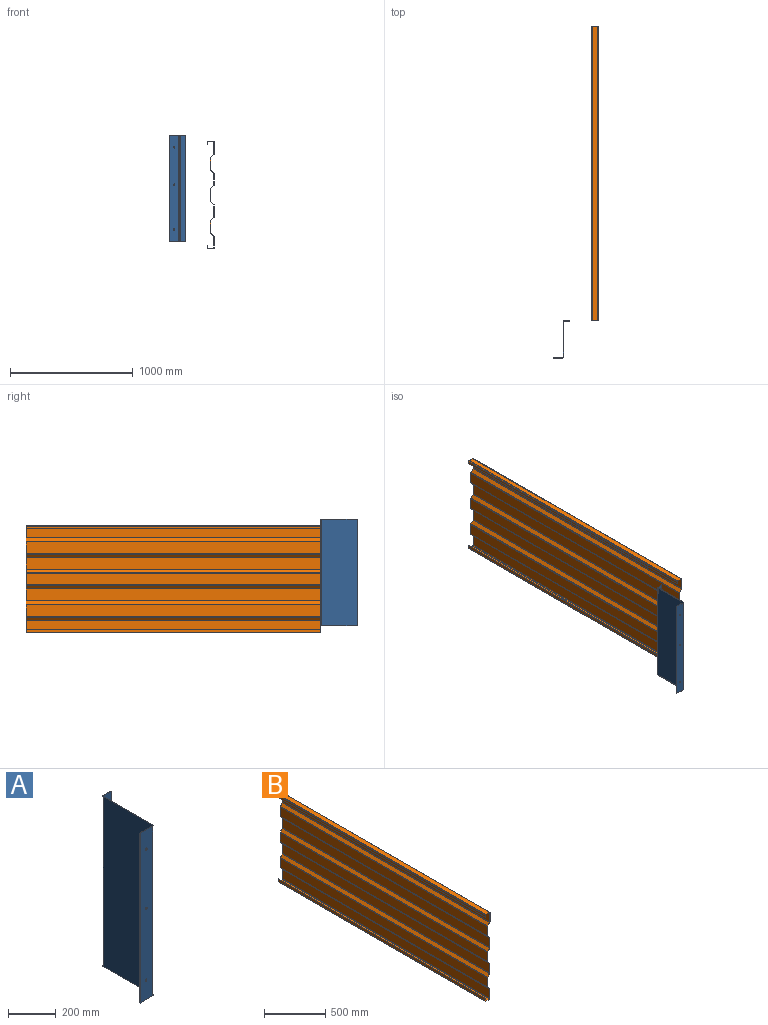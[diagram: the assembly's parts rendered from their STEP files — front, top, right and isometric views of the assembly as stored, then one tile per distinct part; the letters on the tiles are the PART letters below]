
ASSEMBLY  parts=2 mates=1
PART A: 25 faces, bbox 130x302x869 mm
  f0: plane 46x2mm, normal (0,0,-1), area 92mm2, adj f2,f3,f4,f22
  f1: plane 46x2mm, normal (0,0,1), area 92mm2, adj f2,f3,f4,f21
  f2: plane 869x2mm, normal (1,0,0), area 1738mm2, adj f0,f1,f3,f4
  f3: plane 869x46mm, normal (0,1,0), area 39974mm2, adj f0,f1,f2,f23
  f4: plane 869x46mm, normal (0,-1,0), area 39974mm2, adj f0,f1,f2,f24
  f5: plane 290x2mm, normal (0,0,-1), area 580mm2, adj f7,f8,f18,f22
  f6: plane 290x2mm, normal (0,0,1), area 580mm2, adj f7,f8,f17,f21
  f7: plane 869x290mm, normal (-1,0,0), area 252010mm2, adj f5,f6,f20,f23
  f8: plane 869x290mm, normal (1,0,0), area 252010mm2, adj f5,f6,f19,f24
  f9: plane 74x2mm, normal (0,0,-1), area 148mm2, adj f10,f15,f16,f18
  f10: plane 869x2mm, normal (-1,0,0), area 1738mm2, adj f9,f11,f15,f16
  f11: plane 74x2mm, normal (0,0,1), area 148mm2, adj f10,f15,f16,f17
  f12: cylinder r=5mm len=10mm, axis (0,1,0), area 62.8mm2, adj f15,f16
  f13: cylinder r=5mm len=10mm, axis (0,1,0), area 62.8mm2, adj f15,f16
  f14: cylinder r=5mm len=10mm, axis (0,1,0), area 62.8mm2, adj f15,f16
  f15: plane 869x74mm, normal (0,1,0), area 64070.4mm2, adj f9,f10,f11,f12,f13,f14,f20
  f16: plane 869x74mm, normal (0,-1,0), area 64070.4mm2, adj f9,f10,f11,f12,f13,f14,f19
  f17: plane 6x6mm, normal (0,0,1), area 15.7mm2, adj f6,f11,f19,f20
  f18: plane 6x6mm, normal (0,0,-1), area 15.7mm2, adj f5,f9,f19,f20
  f19: cylinder r=6mm len=869mm, axis (0,0,1), area 8190.1mm2, adj f8,f16,f17,f18
  f20: cylinder r=4mm len=869mm, axis (0,0,1), area 5460.1mm2, adj f7,f15,f17,f18
  f21: plane 6x6mm, normal (0,0,1), area 15.7mm2, adj f1,f6,f23,f24
  f22: plane 6x6mm, normal (0,0,-1), area 15.7mm2, adj f0,f5,f23,f24
  f23: cylinder r=6mm len=869mm, axis (0,0,1), area 8190.1mm2, adj f3,f7,f21,f22
  f24: cylinder r=4mm len=869mm, axis (0,0,1), area 5460.1mm2, adj f4,f8,f21,f22
PART B: 134 faces, bbox 55.5x2400x874.2 mm
  f0: plane 21x2.5mm, normal (0,1,0), area 52.5mm2, adj f2,f3,f4,f131
  f1: plane 21x2.5mm, normal (0,-1,0), area 52.5mm2, adj f2,f3,f4,f130
  f2: plane 2400x2.5mm, normal (0,0,-1), area 6000mm2, adj f0,f1,f3,f4
  f3: plane 2400x21mm, normal (1,0,0), area 50400mm2, adj f0,f1,f2,f133
  f4: plane 2400x21mm, normal (-1,0,0), area 50400mm2, adj f0,f1,f2,f132
  f5: plane 42x2.5mm, normal (0,1,0), area 105mm2, adj f7,f8,f127,f131
  f6: plane 42x2.5mm, normal (0,-1,0), area 105mm2, adj f7,f8,f126,f130
  f7: plane 2400x42mm, normal (0,0,-1), area 100800mm2, adj f5,f6,f129,f133
  f8: plane 2400x42mm, normal (0,0,1), area 100800mm2, adj f5,f6,f128,f132
  f9: plane 94.3x2.5mm, normal (0,1,0), area 235.8mm2, adj f11,f12,f123,f127
  f10: plane 94.3x2.5mm, normal (0,-1,0), area 235.8mm2, adj f11,f12,f122,f126
  f11: plane 2400x94.3mm, normal (-1,0,0), area 226325mm2, adj f9,f10,f125,f129
  f12: plane 2400x94.3mm, normal (1,0,0), area 226325mm2, adj f9,f10,f124,f128
  f13: plane 27.3x26.49mm, normal (0,1,0), area 88.9mm2, adj f15,f16,f119,f123
  f14: plane 27.3x26.49mm, normal (0,-1,0), area 88.9mm2, adj f15,f16,f118,f122
  f15: plane 2400x25.57mm, normal (-0.69,0,0.72), area 85303.2mm2, adj f13,f14,f120,f125
  f16: plane 2400x25.57mm, normal (0.69,0,-0.72), area 85303.2mm2, adj f13,f14,f121,f124
  f17: plane 94.55x2.5mm, normal (0,1,0), area 236.4mm2, adj f19,f20,f115,f119
  f18: plane 94.55x2.5mm, normal (0,-1,0), area 236.4mm2, adj f19,f20,f114,f118
  f19: plane 2400x94.55mm, normal (-1,0,0), area 226916.5mm2, adj f17,f18,f116,f120
  f20: plane 2400x94.55mm, normal (1,0,0), area 226916.5mm2, adj f17,f18,f117,f121
  f21: plane 26.98x26.98mm, normal (0,1,0), area 89.1mm2, adj f23,f24,f111,f115
  f22: plane 26.98x26.98mm, normal (0,-1,0), area 89.1mm2, adj f23,f24,f110,f114
  f23: plane 2400x25.21mm, normal (-0.71,0,-0.71), area 85561.8mm2, adj f21,f22,f113,f116
  f24: plane 2400x25.21mm, normal (0.71,0,0.71), area 85561.8mm2, adj f21,f22,f112,f117
  f25: plane 96.69x2.5mm, normal (0,1,0), area 241.7mm2, adj f27,f28,f107,f111
  f26: plane 96.69x2.5mm, normal (0,-1,0), area 241.7mm2, adj f27,f28,f106,f110
  f27: plane 2400x96.69mm, normal (-1,0,0), area 232047.1mm2, adj f25,f26,f109,f113
  f28: plane 2400x96.69mm, normal (1,0,0), area 232047.1mm2, adj f25,f26,f108,f112
  f29: plane 26.98x26.98mm, normal (0,1,0), area 89.1mm2, adj f31,f32,f103,f107
  f30: plane 26.98x26.98mm, normal (0,-1,0), area 89.1mm2, adj f31,f32,f102,f106
  f31: plane 2400x25.21mm, normal (-0.71,0,0.71), area 85561.8mm2, adj f29,f30,f104,f109
  f32: plane 2400x25.21mm, normal (0.71,0,-0.71), area 85561.8mm2, adj f29,f30,f105,f108
  f33: plane 94.62x2.5mm, normal (0,1,0), area 236.5mm2, adj f35,f36,f99,f103
  f34: plane 94.62x2.5mm, normal (0,-1,0), area 236.5mm2, adj f35,f36,f98,f102
  f35: plane 2400x94.62mm, normal (-1,0,0), area 227076.5mm2, adj f33,f34,f100,f104
  f36: plane 2400x94.62mm, normal (1,0,0), area 227076.5mm2, adj f33,f34,f101,f105
  f37: plane 26.98x26.98mm, normal (0,1,0), area 89.1mm2, adj f39,f40,f95,f99
  f38: plane 26.98x26.98mm, normal (0,-1,0), area 89.1mm2, adj f39,f40,f94,f98
  f39: plane 2400x25.21mm, normal (-0.71,0,-0.71), area 85561.8mm2, adj f37,f38,f97,f100
  f40: plane 2400x25.21mm, normal (0.71,0,0.71), area 85561.8mm2, adj f37,f38,f96,f101
  f41: plane 96.69x2.5mm, normal (0,1,0), area 241.7mm2, adj f43,f44,f91,f95
  f42: plane 96.69x2.5mm, normal (0,-1,0), area 241.7mm2, adj f43,f44,f90,f94
  f43: plane 2400x96.69mm, normal (-1,0,0), area 232047.1mm2, adj f41,f42,f93,f97
  f44: plane 2400x96.69mm, normal (1,0,0), area 232047.1mm2, adj f41,f42,f92,f96
  f45: plane 26.98x26.98mm, normal (0,1,0), area 89.1mm2, adj f47,f48,f87,f91
  f46: plane 26.98x26.98mm, normal (0,-1,0), area 89.1mm2, adj f47,f48,f86,f90
  f47: plane 2400x25.21mm, normal (-0.71,0,0.71), area 85561.8mm2, adj f45,f46,f88,f93
  f48: plane 2400x25.21mm, normal (0.71,0,-0.71), area 85561.8mm2, adj f45,f46,f89,f92
  f49: plane 94.62x2.5mm, normal (0,1,0), area 236.5mm2, adj f51,f52,f83,f87
  f50: plane 94.62x2.5mm, normal (0,-1,0), area 236.5mm2, adj f51,f52,f82,f86
  f51: plane 2400x94.62mm, normal (-1,0,0), area 227076.5mm2, adj f49,f50,f84,f88
  f52: plane 2400x94.62mm, normal (1,0,0), area 227076.5mm2, adj f49,f50,f85,f89
  f53: plane 26.98x26.98mm, normal (0,1,0), area 89.1mm2, adj f55,f56,f79,f83
  f54: plane 26.98x26.98mm, normal (0,-1,0), area 89.1mm2, adj f55,f56,f78,f82
  f55: plane 2400x25.21mm, normal (-0.71,0,-0.71), area 85561.8mm2, adj f53,f54,f81,f84
  f56: plane 2400x25.21mm, normal (0.71,0,0.71), area 85561.8mm2, adj f53,f54,f80,f85
  f57: plane 94.34x2.5mm, normal (0,1,0), area 235.9mm2, adj f59,f60,f75,f79
  f58: plane 94.34x2.5mm, normal (0,-1,0), area 235.9mm2, adj f59,f60,f74,f78
  f59: plane 2400x94.34mm, normal (-1,0,0), area 226423.6mm2, adj f57,f58,f77,f81
  f60: plane 2400x94.34mm, normal (1,0,0), area 226423.6mm2, adj f57,f58,f76,f80
  f61: plane 42x2.5mm, normal (0,1,0), area 105mm2, adj f63,f64,f71,f75
  f62: plane 42x2.5mm, normal (0,-1,0), area 105mm2, adj f63,f64,f70,f74
  f63: plane 2400x42mm, normal (0,0,1), area 100800mm2, adj f61,f62,f73,f77
  f64: plane 2400x42mm, normal (0,0,-1), area 100800mm2, adj f61,f62,f72,f76
  f65: plane 24.58x2.5mm, normal (0,1,0), area 61.4mm2, adj f66,f68,f69,f71
  f66: plane 2400x2.5mm, normal (0,0,1), area 6000mm2, adj f65,f67,f68,f69
  f67: plane 24.58x2.5mm, normal (0,-1,0), area 61.4mm2, adj f66,f68,f69,f70
  f68: plane 2400x24.58mm, normal (1,0,0), area 58991.7mm2, adj f65,f66,f67,f73
  f69: plane 2400x24.58mm, normal (-1,0,0), area 58991.7mm2, adj f65,f66,f67,f72
  f70: plane 6.5x6.5mm, normal (0,-1,0), area 20.6mm2, adj f62,f67,f72,f73
  f71: plane 6.5x6.5mm, normal (0,1,0), area 20.6mm2, adj f61,f65,f72,f73
  f72: cylinder r=6.5mm len=2400mm, axis (0,-1,0), area 24504.4mm2, adj f64,f69,f70,f71
  f73: cylinder r=4mm len=2400mm, axis (0,-1,0), area 15079.6mm2, adj f63,f68,f70,f71
  f74: plane 6.5x6.5mm, normal (0,-1,0), area 20.6mm2, adj f58,f62,f76,f77
  f75: plane 6.5x6.5mm, normal (0,1,0), area 20.6mm2, adj f57,f61,f76,f77
  f76: cylinder r=6.5mm len=2400mm, axis (0,-1,0), area 24504.4mm2, adj f60,f64,f74,f75
  f77: cylinder r=4mm len=2400mm, axis (0,-1,0), area 15079.6mm2, adj f59,f63,f74,f75
  f78: plane 4.6x3.67mm, normal (0,-1,0), area 10.3mm2, adj f54,f58,f80,f81
  f79: plane 4.6x3.67mm, normal (0,1,0), area 10.3mm2, adj f53,f57,f80,f81
  f80: cylinder r=6.5mm len=2400mm, axis (0,-1,0), area 12252.2mm2, adj f56,f60,f78,f79
  f81: cylinder r=4mm len=2400mm, axis (0,-1,0), area 7539.8mm2, adj f55,f59,f78,f79
  f82: plane 4.6x3.67mm, normal (0,-1,0), area 10.3mm2, adj f50,f54,f84,f85
  f83: plane 4.6x3.67mm, normal (0,1,0), area 10.3mm2, adj f49,f53,f84,f85
  f84: cylinder r=6.5mm len=2400mm, axis (0,-1,0), area 12252.2mm2, adj f51,f55,f82,f83
  f85: cylinder r=4mm len=2400mm, axis (0,-1,0), area 7539.8mm2, adj f52,f56,f82,f83
  f86: plane 4.6x3.67mm, normal (0,-1,0), area 10.3mm2, adj f46,f50,f88,f89
  f87: plane 4.6x3.67mm, normal (0,1,0), area 10.3mm2, adj f45,f49,f88,f89
  f88: cylinder r=6.5mm len=2400mm, axis (0,-1,0), area 12252.2mm2, adj f47,f51,f86,f87
  f89: cylinder r=4mm len=2400mm, axis (0,-1,0), area 7539.8mm2, adj f48,f52,f86,f87
  f90: plane 4.6x3.67mm, normal (0,-1,0), area 10.3mm2, adj f42,f46,f92,f93
  f91: plane 4.6x3.67mm, normal (0,1,0), area 10.3mm2, adj f41,f45,f92,f93
  f92: cylinder r=6.5mm len=2400mm, axis (0,-1,0), area 12252.2mm2, adj f44,f48,f90,f91
  f93: cylinder r=4mm len=2400mm, axis (0,-1,0), area 7539.8mm2, adj f43,f47,f90,f91
  f94: plane 4.6x3.67mm, normal (0,-1,0), area 10.3mm2, adj f38,f42,f96,f97
  f95: plane 4.6x3.67mm, normal (0,1,0), area 10.3mm2, adj f37,f41,f96,f97
  f96: cylinder r=6.5mm len=2400mm, axis (0,-1,0), area 12252.2mm2, adj f40,f44,f94,f95
  f97: cylinder r=4mm len=2400mm, axis (0,-1,0), area 7539.8mm2, adj f39,f43,f94,f95
  f98: plane 4.6x3.67mm, normal (0,-1,0), area 10.3mm2, adj f34,f38,f100,f101
  f99: plane 4.6x3.67mm, normal (0,1,0), area 10.3mm2, adj f33,f37,f100,f101
  f100: cylinder r=6.5mm len=2400mm, axis (0,-1,0), area 12252.2mm2, adj f35,f39,f98,f99
  f101: cylinder r=4mm len=2400mm, axis (0,-1,0), area 7539.8mm2, adj f36,f40,f98,f99
  f102: plane 4.6x3.67mm, normal (0,-1,0), area 10.3mm2, adj f30,f34,f104,f105
  f103: plane 4.6x3.67mm, normal (0,1,0), area 10.3mm2, adj f29,f33,f104,f105
  f104: cylinder r=6.5mm len=2400mm, axis (0,-1,0), area 12252.2mm2, adj f31,f35,f102,f103
  f105: cylinder r=4mm len=2400mm, axis (0,-1,0), area 7539.8mm2, adj f32,f36,f102,f103
  f106: plane 4.6x3.67mm, normal (0,-1,0), area 10.3mm2, adj f26,f30,f108,f109
  f107: plane 4.6x3.67mm, normal (0,1,0), area 10.3mm2, adj f25,f29,f108,f109
  f108: cylinder r=6.5mm len=2400mm, axis (0,-1,0), area 12252.2mm2, adj f28,f32,f106,f107
  f109: cylinder r=4mm len=2400mm, axis (0,-1,0), area 7539.8mm2, adj f27,f31,f106,f107
  f110: plane 4.6x3.67mm, normal (0,-1,0), area 10.3mm2, adj f22,f26,f112,f113
  f111: plane 4.6x3.67mm, normal (0,1,0), area 10.3mm2, adj f21,f25,f112,f113
  f112: cylinder r=6.5mm len=2400mm, axis (0,-1,0), area 12252.2mm2, adj f24,f28,f110,f111
  f113: cylinder r=4mm len=2400mm, axis (0,-1,0), area 7539.8mm2, adj f23,f27,f110,f111
  f114: plane 4.6x3.67mm, normal (0,-1,0), area 10.3mm2, adj f18,f22,f116,f117
  f115: plane 4.6x3.67mm, normal (0,1,0), area 10.3mm2, adj f17,f21,f116,f117
  f116: cylinder r=6.5mm len=2400mm, axis (0,-1,0), area 12252.2mm2, adj f19,f23,f114,f115
  f117: cylinder r=4mm len=2400mm, axis (0,-1,0), area 7539.8mm2, adj f20,f24,f114,f115
  f118: plane 4.68x3.72mm, normal (0,-1,0), area 10.5mm2, adj f14,f18,f120,f121
  f119: plane 4.68x3.72mm, normal (0,1,0), area 10.5mm2, adj f13,f17,f120,f121
  f120: cylinder r=6.5mm len=2400mm, axis (0,-1,0), area 12524.5mm2, adj f15,f19,f118,f119
  f121: cylinder r=4mm len=2400mm, axis (0,-1,0), area 7707.4mm2, adj f16,f20,f118,f119
  f122: plane 4.68x3.72mm, normal (0,-1,0), area 10.5mm2, adj f10,f14,f124,f125
  f123: plane 4.68x3.72mm, normal (0,1,0), area 10.5mm2, adj f9,f13,f124,f125
  f124: cylinder r=6.5mm len=2400mm, axis (0,-1,0), area 12524.5mm2, adj f12,f16,f122,f123
  f125: cylinder r=4mm len=2400mm, axis (0,-1,0), area 7707.4mm2, adj f11,f15,f122,f123
  f126: plane 6.5x6.5mm, normal (0,-1,0), area 20.6mm2, adj f6,f10,f128,f129
  f127: plane 6.5x6.5mm, normal (0,1,0), area 20.6mm2, adj f5,f9,f128,f129
  f128: cylinder r=6.5mm len=2400mm, axis (0,-1,0), area 24504.4mm2, adj f8,f12,f126,f127
  f129: cylinder r=4mm len=2400mm, axis (0,-1,0), area 15079.6mm2, adj f7,f11,f126,f127
  f130: plane 6.5x6.5mm, normal (0,-1,0), area 20.6mm2, adj f1,f6,f132,f133
  f131: plane 6.5x6.5mm, normal (0,1,0), area 20.6mm2, adj f0,f5,f132,f133
  f132: cylinder r=6.5mm len=2400mm, axis (0,-1,0), area 24504.4mm2, adj f4,f8,f130,f131
  f133: cylinder r=4mm len=2400mm, axis (0,-1,0), area 15079.6mm2, adj f3,f7,f130,f131
PLACE A t=(-1477.64,-1666.61,239.78)mm
PLACE B t=(-1194.2,912.37,833.31)mm fixed
MATE planar A.f3 <-> B.f18  axis (0,1,0) through (-1439.54,-1487.63,674.28)mm
